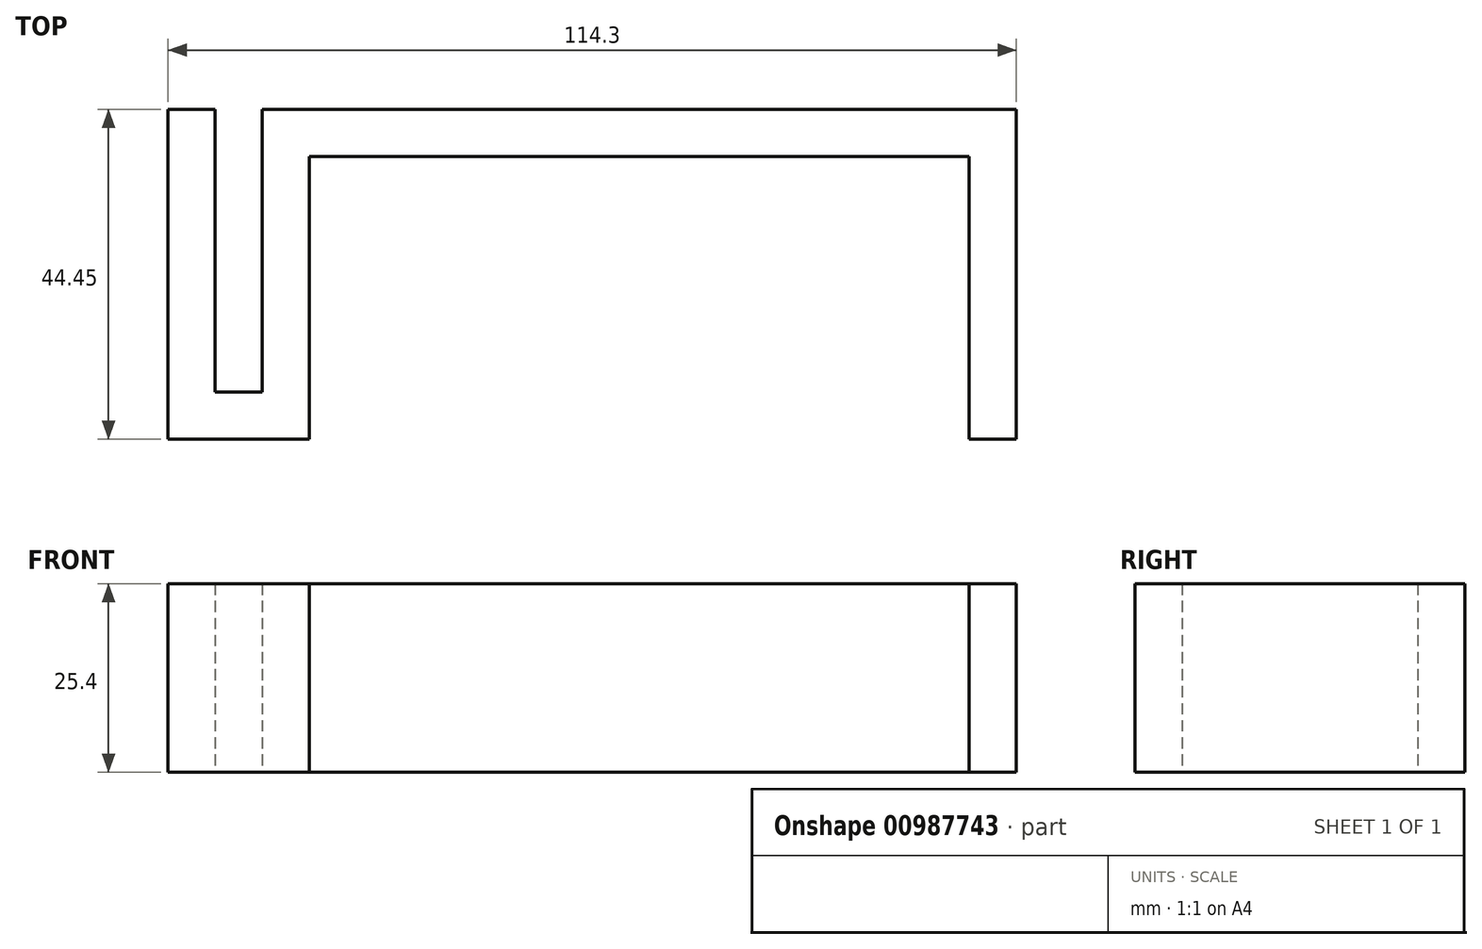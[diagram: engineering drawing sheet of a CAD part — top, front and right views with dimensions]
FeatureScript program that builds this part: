
annotation { "Feature Type Name" : "Feature", "Feature Type Description" : "" }
export const myFeature = defineFeature(function(context is Context, id is Id, definition is map)
    precondition{}
    {
        {
            var Q0;
            Q0=qCreatedBy(makeId("Top.planeOp"),FACE);
            var sketch = newSketch(context, id + "F0", { "sketchPlane" : qUnion([Q0])});
            skLineSegment(sketch, "E0.bottom", {"start": v(44.45, -19.05) * mm, "end": v(-44.45, -19.05) * mm});
            skLineSegment(sketch, "E0.top", {"start": v(44.45, 19.05) * mm, "end": v(-44.45, 19.05) * mm});
            skLineSegment(sketch, "E0.left", {"start": v(44.45, -19.05) * mm, "end": v(44.45, 19.05) * mm});
            skLineSegment(sketch, "E0.right", {"start": v(-44.45, -19.05) * mm, "end": v(-44.45, 19.05) * mm});
            skPoint(sketch, "E0.middle", {"position": v(0, 0) * mm});
            skLineSegment(sketch, "E1.bottom", {"start": v(44.45, -19.05) * mm, "end": v(50.8, -19.05) * mm});
            skLineSegment(sketch, "E1.top", {"start": v(44.45, 25.4) * mm, "end": v(50.8, 25.4) * mm});
            skLineSegment(sketch, "E1.left", {"start": v(44.45, -19.05) * mm, "end": v(44.45, 25.4) * mm});
            skLineSegment(sketch, "E1.right", {"start": v(50.8, -19.05) * mm, "end": v(50.8, 25.4) * mm});
            skLineSegment(sketch, "E2.bottom", {"start": v(44.45, 25.4) * mm, "end": v(-50.8, 25.4) * mm});
            skLineSegment(sketch, "E2.top", {"start": v(44.45, 19.05) * mm, "end": v(-50.8, 19.05) * mm});
            skLineSegment(sketch, "E2.left", {"start": v(44.45, 25.4) * mm, "end": v(44.45, 19.05) * mm});
            skLineSegment(sketch, "E2.right", {"start": v(-50.8, 25.4) * mm, "end": v(-50.8, 19.05) * mm});
            skLineSegment(sketch, "E3.bottom", {"start": v(-50.8, 19.05) * mm, "end": v(-44.45, 19.05) * mm});
            skLineSegment(sketch, "E3.top", {"start": v(-50.8, -19.05) * mm, "end": v(-44.45, -19.05) * mm});
            skLineSegment(sketch, "E3.left", {"start": v(-50.8, 19.05) * mm, "end": v(-50.8, -19.05) * mm});
            skLineSegment(sketch, "E3.right", {"start": v(-44.45, 19.05) * mm, "end": v(-44.45, -19.05) * mm});
            skLineSegment(sketch, "E4.bottom", {"start": v(-50.8, -19.05) * mm, "end": v(-63.5, -19.05) * mm});
            skLineSegment(sketch, "E4.top", {"start": v(-50.8, -12.7) * mm, "end": v(-63.5, -12.7) * mm});
            skLineSegment(sketch, "E4.left", {"start": v(-50.8, -19.05) * mm, "end": v(-50.8, -12.7) * mm});
            skLineSegment(sketch, "E4.right", {"start": v(-63.5, -19.05) * mm, "end": v(-63.5, -12.7) * mm});
            skLineSegment(sketch, "E5.bottom", {"start": v(-63.5, -12.7) * mm, "end": v(-57.15, -12.7) * mm});
            skLineSegment(sketch, "E5.top", {"start": v(-63.5, 25.4) * mm, "end": v(-57.15, 25.4) * mm});
            skLineSegment(sketch, "E5.left", {"start": v(-63.5, -12.7) * mm, "end": v(-63.5, 25.4) * mm});
            skLineSegment(sketch, "E5.right", {"start": v(-57.15, -12.7) * mm, "end": v(-57.15, 25.4) * mm});
            skSolve(sketch);
        }
        {
            var Q0;
            Q0=makeQuery(id+"F0.imprint","IMPRINT",FACE,{"disambiguationData":[TD([[makeQuery(id+"F0.imprint","IMPRINT",EDGE,{"derivedFrom":sQuery(id+"F0.wireOp",EDGE,"E5.top")}),-1.0]])]});
            var Q1;
            {var subQ5=sQuery(id+"F0.wireOp",EDGE,"E4.bottom");Q1=makeQuery(id+"F0.imprint","IMPRINT",FACE,{"disambiguationData":[TD([[makeQuery(id+"F0.imprint","IMPRINT",EDGE,{"derivedFrom":subQ5}),-1.0]])]});}
            var Q2;
            Q2=makeQuery(id+"F0.imprint","IMPRINT",FACE,{"disambiguationData":[TD([[makeQuery(id+"F0.imprint","IMPRINT",EDGE,{"derivedFrom":sQuery(id+"F0.wireOp",EDGE,"E0.right")}),1.0]])]});
            var Q3;
            Q3=makeQuery(id+"F0.imprint","IMPRINT",FACE,{"disambiguationData":[TD([[makeQuery(id+"F0.imprint","IMPRINT",EDGE,{"derivedFrom":sQuery(id+"F0.wireOp",EDGE,"E0.top")}),-1.0]])]});
            var Q4;
            Q4=makeQuery(id+"F0.imprint","IMPRINT",FACE,{"disambiguationData":[TD([[makeQuery(id+"F0.imprint","IMPRINT",EDGE,{"derivedFrom":sQuery(id+"F0.wireOp",EDGE,"E0.left")}),-1.0]])]});
            extrude(context, id + "F1", {"entities" : qUnion([Q0, Q1, Q2, Q3, Q4]), "depth" : 25.4 * mm, "offsetDistance" : 25.4 * mm});
        }
    });
